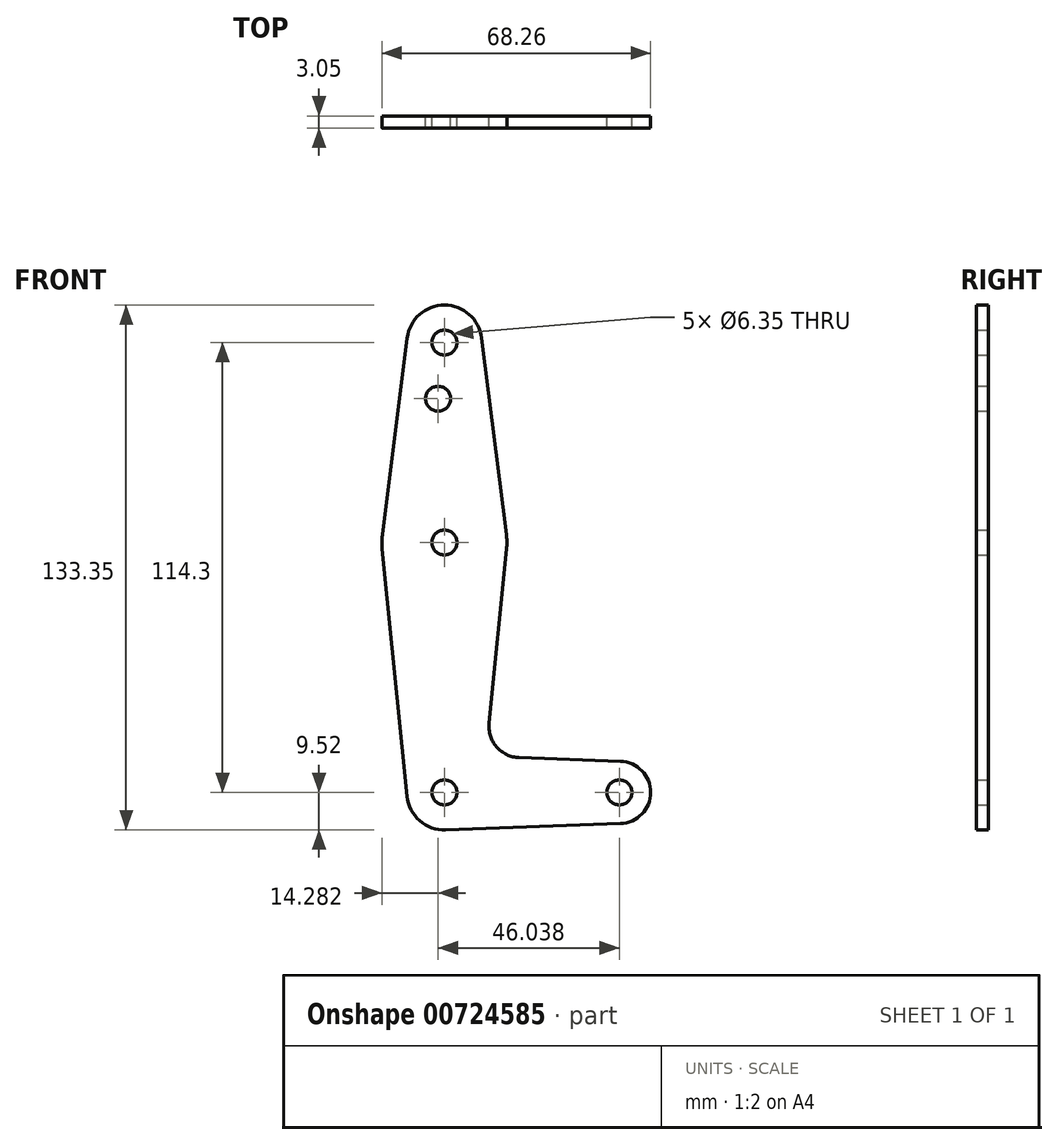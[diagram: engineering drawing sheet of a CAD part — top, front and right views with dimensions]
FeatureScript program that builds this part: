
annotation { "Feature Type Name" : "Feature", "Feature Type Description" : "" }
export const myFeature = defineFeature(function(context is Context, id is Id, definition is map)
    precondition{}
    {
        {
            var Q0;
            Q0=qCreatedBy(makeId("Front.planeOp"),FACE);
            var sketch = newSketch(context, id + "F0", { "sketchPlane" : qUnion([Q0])});
            skLineSegment(sketch, "E0", {"start": v(0, 0) * mm, "end": v(0, 114.3) * mm, "construction": true});
            skLineSegment(sketch, "E1", {"start": v(44.45, 0) * mm, "end": v(0, 0) * mm, "construction": true});
            skCircle(sketch, "E2", {"center": v(0, 114.3) * mm, "radius": 9.53 * mm});
            skCircle(sketch, "E3", {"center": v(0, 0) * mm, "radius": 9.53 * mm});
            skCircle(sketch, "E4", {"center": v(44.45, 0) * mm, "radius": 7.94 * mm});
            skCircle(sketch, "E5", {"center": v(0, 63.5) * mm, "radius": 15.88 * mm});
            skLineSegment(sketch, "E6", {"start": v(9.45, 115.5) * mm, "end": v(15.75, 65.48) * mm});
            skLineSegment(sketch, "E7", {"start": v(-9.45, 115.5) * mm, "end": v(-15.75, 65.48) * mm});
            skLineSegment(sketch, "E8", {"start": v(18.97, 8.85) * mm, "end": v(44.73, 7.93) * mm});
            skLineSegment(sketch, "E9", {"start": v(0.34, -9.52) * mm, "end": v(44.73, -7.93) * mm});
            skCircle(sketch, "E10", {"center": v(0, 114.3) * mm, "radius": 3.18 * mm});
            skCircle(sketch, "E11", {"center": v(-1.59, 100.03) * mm, "radius": 3.18 * mm});
            skCircle(sketch, "E12", {"center": v(0, 63.5) * mm, "radius": 3.18 * mm});
            skCircle(sketch, "E13", {"center": v(0, 0) * mm, "radius": 3.18 * mm});
            skCircle(sketch, "E14", {"center": v(44.45, 0) * mm, "radius": 3.18 * mm});
            skLineSegment(sketch, "E15", {"start": v(-15.8, 61.91) * mm, "end": v(-9.48, -0.95) * mm});
            skLineSegment(sketch, "E16", {"start": v(15.8, 61.91) * mm, "end": v(11.34, 17.6) * mm});
            skArc(sketch, "E17.filletArc", {"start": v(11.34, 17.6) * mm, "mid": v(13.26, 11.57) * mm, "end": v(18.97, 8.85) * mm});
            skSolve(sketch);
        }
        {
            var Q0;
            Q0 = qSketchRegion(id + "F0", true);
            extrude(context, id + "F1", {"entities" : qUnion([Q0]), "depth" : 3.05 * mm, "offsetDistance" : 25.4 * mm});
        }
    });
